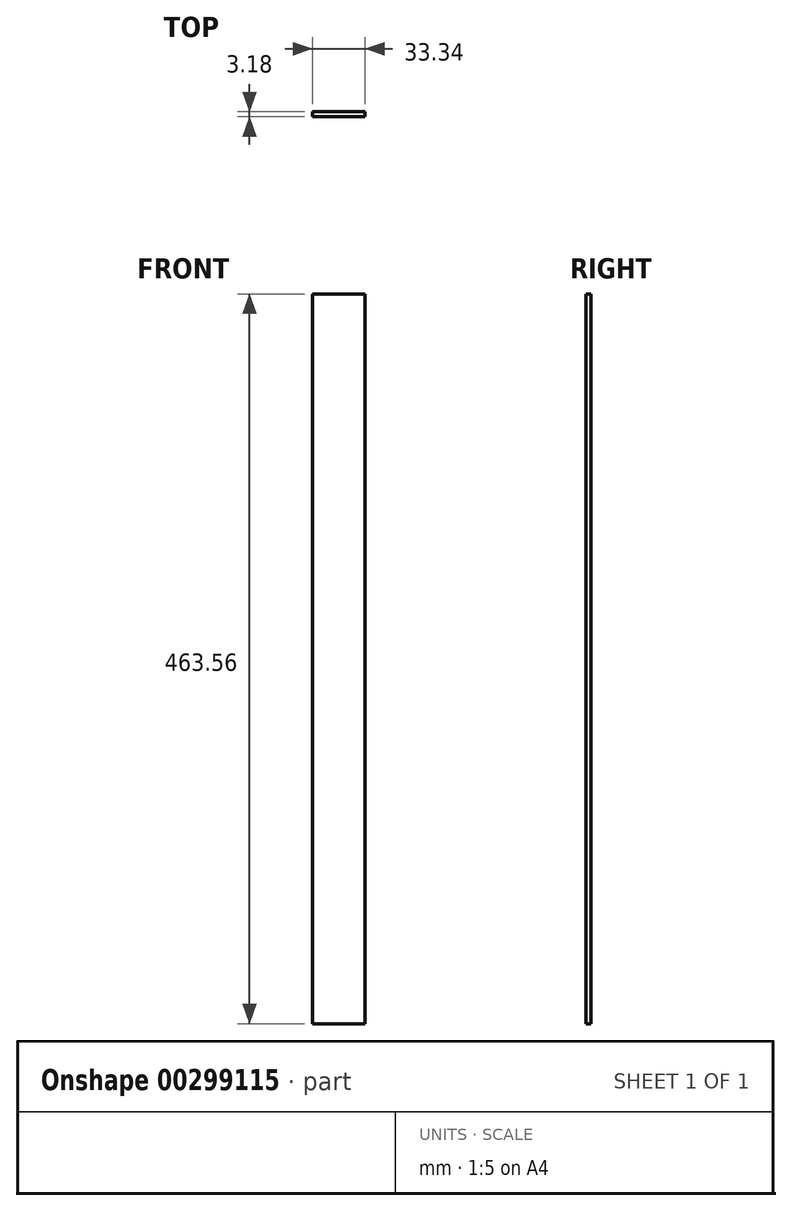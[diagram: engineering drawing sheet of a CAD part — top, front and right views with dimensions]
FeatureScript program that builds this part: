
annotation { "Feature Type Name" : "Feature", "Feature Type Description" : "" }
export const myFeature = defineFeature(function(context is Context, id is Id, definition is map)
    precondition{}
    {
        {
            var Q0;
            Q0=qCreatedBy(makeId("Top.planeOp"),FACE);
            var sketch = newSketch(context, id + "F0", { "sketchPlane" : qUnion([Q0])});
            skLineSegment(sketch, "E0.bottom", {"start": v(16.67, 1.59) * mm, "end": v(-16.67, 1.59) * mm});
            skLineSegment(sketch, "E0.top", {"start": v(16.67, -1.59) * mm, "end": v(-16.67, -1.59) * mm});
            skLineSegment(sketch, "E0.left", {"start": v(16.67, 1.59) * mm, "end": v(16.67, -1.59) * mm});
            skLineSegment(sketch, "E0.right", {"start": v(-16.67, 1.59) * mm, "end": v(-16.67, -1.59) * mm});
            skPoint(sketch, "E0.middle", {"position": v(0, 0) * mm});
            skSolve(sketch);
        }
        {
            var Q0;
            Q0 = qSketchRegion(id + "F0", true);
            extrude(context, id + "F1", {"entities" : qUnion([Q0]), "endBound" : BoundingType.SYMMETRIC, "depth" : 463.55 * mm});
        }
    });
